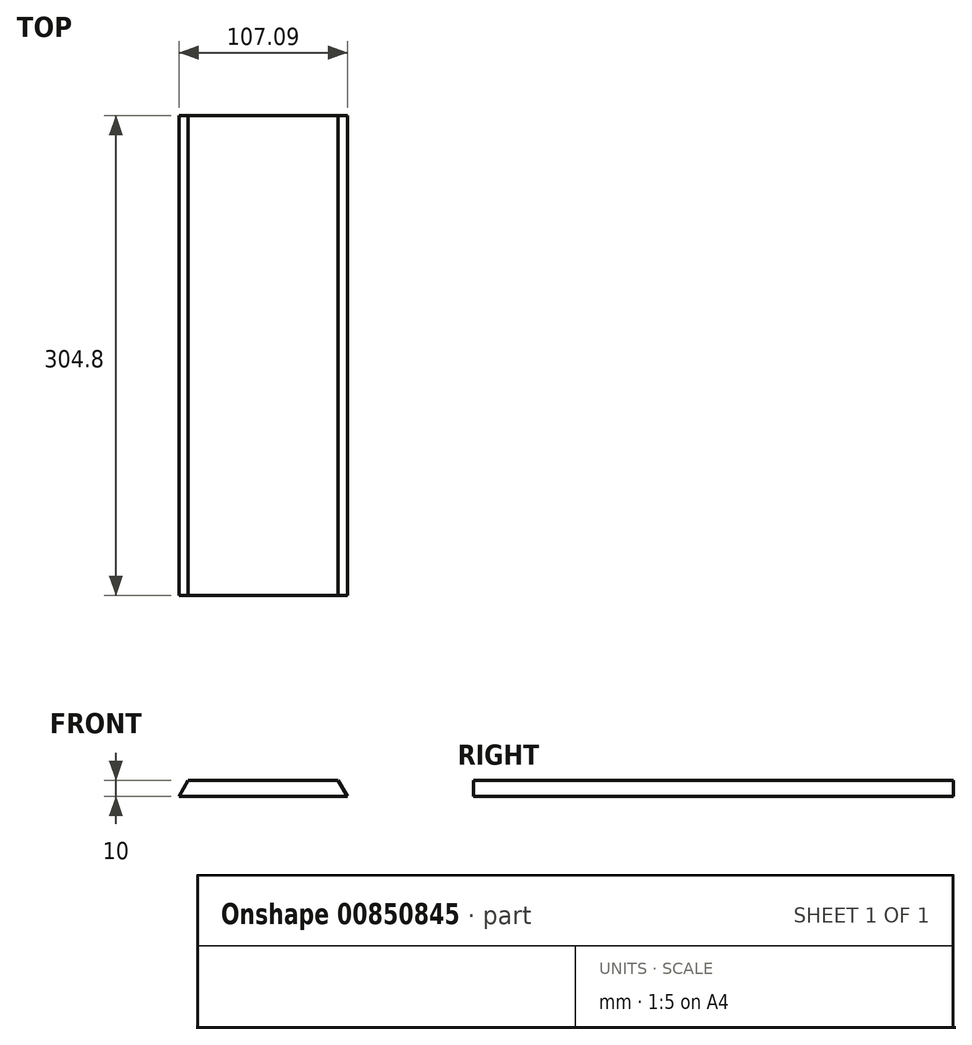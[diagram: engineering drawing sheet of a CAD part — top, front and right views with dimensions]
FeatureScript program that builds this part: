
annotation { "Feature Type Name" : "Feature", "Feature Type Description" : "" }
export const myFeature = defineFeature(function(context is Context, id is Id, definition is map)
    precondition{}
    {
        {
            var Q0;
            Q0=qCreatedBy(makeId("Front.planeOp"),FACE);
            var sketch = newSketch(context, id + "F0", { "sketchPlane" : qUnion([Q0])});
            skLineSegment(sketch, "E0", {"start": v(-131.37, -40.69) * mm, "end": v(-24.28, -40.69) * mm});
            skLineSegment(sketch, "E1", {"start": v(-125.52, -30.69) * mm, "end": v(-131.37, -40.69) * mm});
            skLineSegment(sketch, "E2", {"start": v(-30.14, -30.69) * mm, "end": v(-24.28, -40.69) * mm});
            skLineSegment(sketch, "E3", {"start": v(-125.52, -30.69) * mm, "end": v(-30.14, -30.69) * mm});
            skSolve(sketch);
        }
        {
            var Q0;
            Q0=makeQuery(id+"F0.imprint","IMPRINT",FACE,{"disambiguationData":[TD([[makeQuery(id+"F0.imprint","IMPRINT",EDGE,{"derivedFrom":sQuery(id+"F0.wireOp",EDGE,"E0")}),1.0]])]});
            extrude(context, id + "F1", {"entities" : qUnion([Q0]), "depth" : 304.8 * mm, "offsetDistance" : 25.4 * mm});
        }
    });
